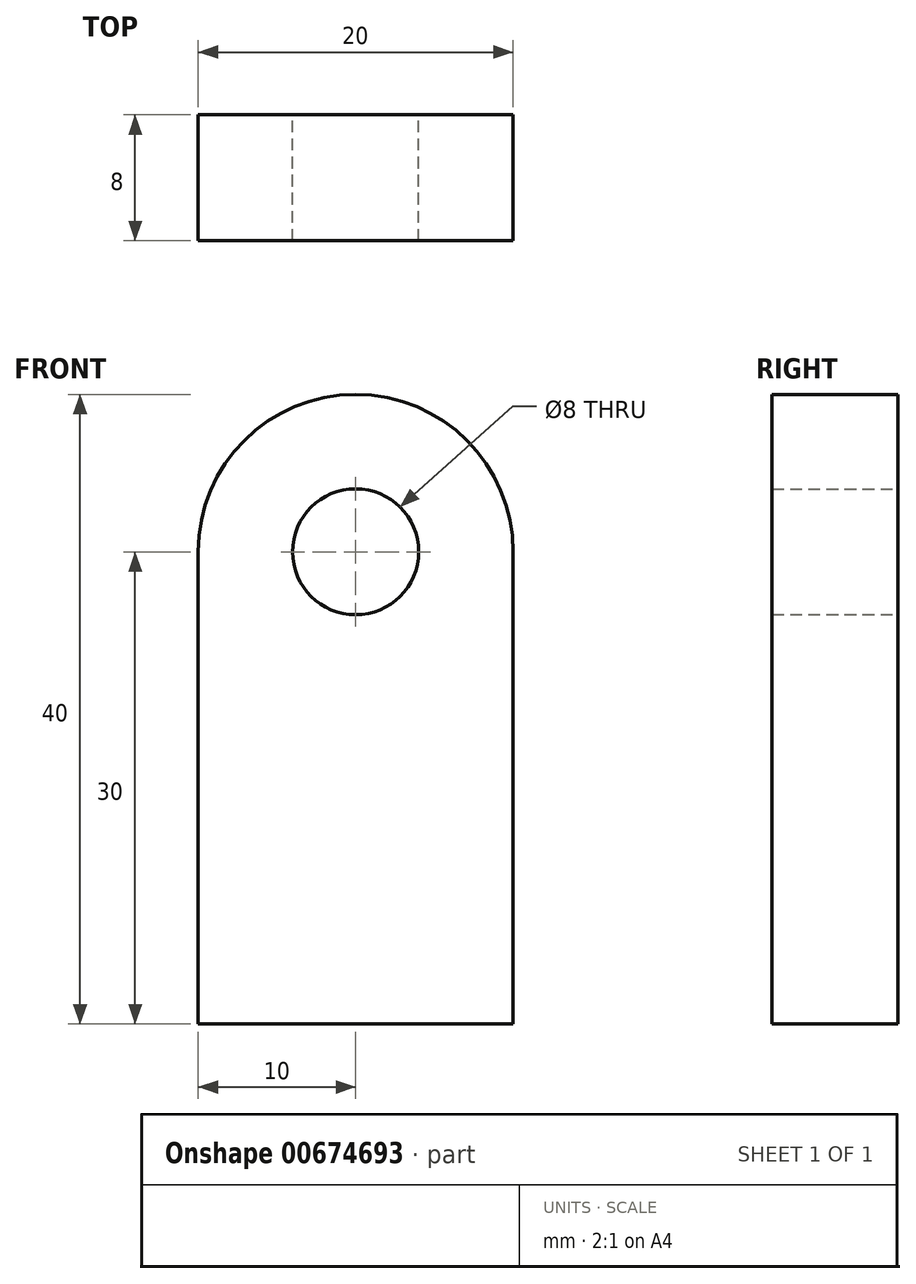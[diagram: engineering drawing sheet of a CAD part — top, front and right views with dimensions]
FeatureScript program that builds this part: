
annotation { "Feature Type Name" : "Feature", "Feature Type Description" : "" }
export const myFeature = defineFeature(function(context is Context, id is Id, definition is map)
    precondition{}
    {
        {
            var Q0;
            Q0=qCreatedBy(makeId("Front.planeOp"),FACE);
            var sketch = newSketch(context, id + "F0", { "sketchPlane" : qUnion([Q0])});
            skLineSegment(sketch, "E0.bottom", {"start": v(0, 0) * mm, "end": v(20, 0) * mm});
            skLineSegment(sketch, "E0.left", {"start": v(0, 0) * mm, "end": v(0, 30) * mm});
            skLineSegment(sketch, "E0.right", {"start": v(20, 0) * mm, "end": v(20, 30) * mm});
            skArc(sketch, "E1", {"start": v(20, 30) * mm, "mid": v(10, 40) * mm, "end": v(0, 30) * mm});
            skCircle(sketch, "E2", {"center": v(10, 30) * mm, "radius": 4 * mm});
            skSolve(sketch);
        }
        {
            var Q0;
            Q0 = qSketchRegion(id + "F0", true);
            extrude(context, id + "F1", {"entities" : qUnion([Q0]), "depth" : 8 * mm, "offsetDistance" : 25 * mm});
        }
    });
